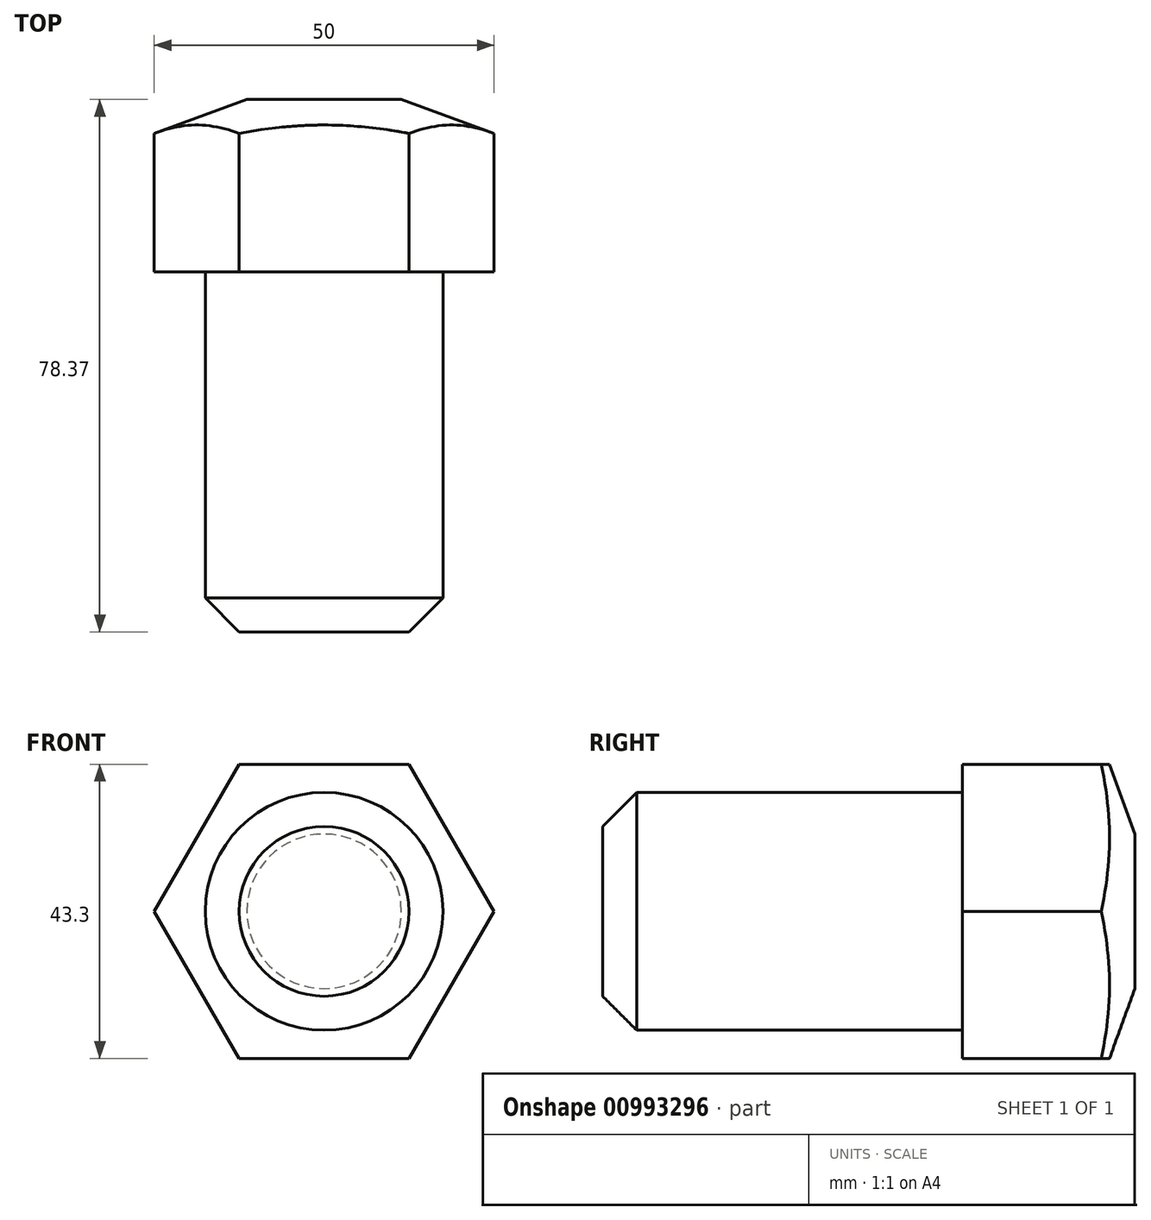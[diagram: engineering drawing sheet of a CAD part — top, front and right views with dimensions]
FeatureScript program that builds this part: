
annotation { "Feature Type Name" : "Feature", "Feature Type Description" : "" }
export const myFeature = defineFeature(function(context is Context, id is Id, definition is map)
    precondition{}
    {
        {
            var Q0;
            Q0=qCreatedBy(makeId("Front.planeOp"),FACE);
            var sketch = newSketch(context, id + "F0", { "sketchPlane" : qUnion([Q0])});
            skCircle(sketch, "E0.cCircle", {"center": v(0, 0) * mm, "radius": 25 * mm, "construction": true});
            skLineSegment(sketch, "E0.0", {"start": v(25, 0) * mm, "end": v(12.5, -21.65) * mm});
            skLineSegment(sketch, "E0.1", {"start": v(12.5, -21.65) * mm, "end": v(-12.5, -21.65) * mm});
            skLineSegment(sketch, "E0.2", {"start": v(-12.5, -21.65) * mm, "end": v(-25, 0) * mm});
            skLineSegment(sketch, "E0.3", {"start": v(-25, 0) * mm, "end": v(-12.5, 21.65) * mm});
            skLineSegment(sketch, "E0.4", {"start": v(-12.5, 21.65) * mm, "end": v(12.5, 21.65) * mm});
            skLineSegment(sketch, "E0.5", {"start": v(12.5, 21.65) * mm, "end": v(25, 0) * mm});
            skSolve(sketch);
        }
        {
            var Q0;
            Q0 = qSketchRegion(id + "F0", true);
            extrude(context, id + "F1", {"entities" : qUnion([Q0]), "oppositeDirection" : true, "depth" : 25.4 * mm, "offsetDistance" : 25.4 * mm});
        }
        {
            var Q0;
            Q0=qCreatedBy(makeId("Front.planeOp"),FACE);
            var sketch = newSketch(context, id + "F2", { "sketchPlane" : qUnion([Q0])});
            skCircle(sketch, "E1", {"center": v(0, 0) * mm, "radius": 17.5 * mm});
            skSolve(sketch);
        }
        {
            var Q0;
            Q0=makeQuery(id+"F2.imprint","IMPRINT",FACE,{"disambiguationData":[TD([[makeQuery(id+"F2.imprint","IMPRINT",EDGE,{"derivedFrom":sQuery(id+"F2.wireOp",EDGE,"E1")}),1.0]])]});
            extrude(context, id + "F3", {"entities" : qUnion([Q0]), "depth" : 52.97 * mm, "offsetDistance" : 25 * mm});
        }
        {
            var Q0;
            Q0=qCreatedBy(makeId("Top.planeOp"),FACE);
            var sketch = newSketch(context, id + "F4", { "sketchPlane" : qUnion([Q0])});
            skLineSegment(sketch, "E2", {"start": v(-35, 16.8) * mm, "end": v(-10, 25.9) * mm});
            skLineSegment(sketch, "E3", {"start": v(-10, 35) * mm, "end": v(-35, 35) * mm});
            skLineSegment(sketch, "E4", {"start": v(-35, 35) * mm, "end": v(-35, 16.8) * mm});
            skLineSegment(sketch, "E5", {"start": v(-10, 35) * mm, "end": v(-10, 25.9) * mm});
            skPoint(sketch, "E6.orphan", {"position": v(15, 35) * mm});
            skSolve(sketch);
        }
        {
            var Q0;
            Q0=makeQuery(id+"F4.imprint","IMPRINT",FACE,{"disambiguationData":[TD([[makeQuery(id+"F4.imprint","IMPRINT",EDGE,{"derivedFrom":sQuery(id+"F4.wireOp",EDGE,"E2")}),1.0]])]});
            var Q1;
            Q1=makeQuery(id+"F3.opExtrude","SWEPT_FACE",FACE,{"disambiguationData":[OSD([sQuery(id+"F2.wireOp",EDGE,"E1")])]});
            revolve(context, id + "F5", {"operationType" : NewBodyOperationType.REMOVE, "surfaceOperationType" : NewSurfaceOperationType.NEW, "entities" : qUnion([Q0]), "axis" : qUnion([Q1]), "revolveType" : RevolveType.FULL, "oppositeDirection" : true});
        }
        {
            var Q0;
            Q0=makeQuery(id+"F3.opExtrude","CAP_EDGE",EDGE,{"disambiguationData":[OSD([sQuery(id+"F2.wireOp",EDGE,"E1")])],"isStart":false});
            chamfer(context, id + "F6", {"entities" : qUnion([Q0]), "width" : 5 * mm, "tangentPropagation" : true});
        }
    });
